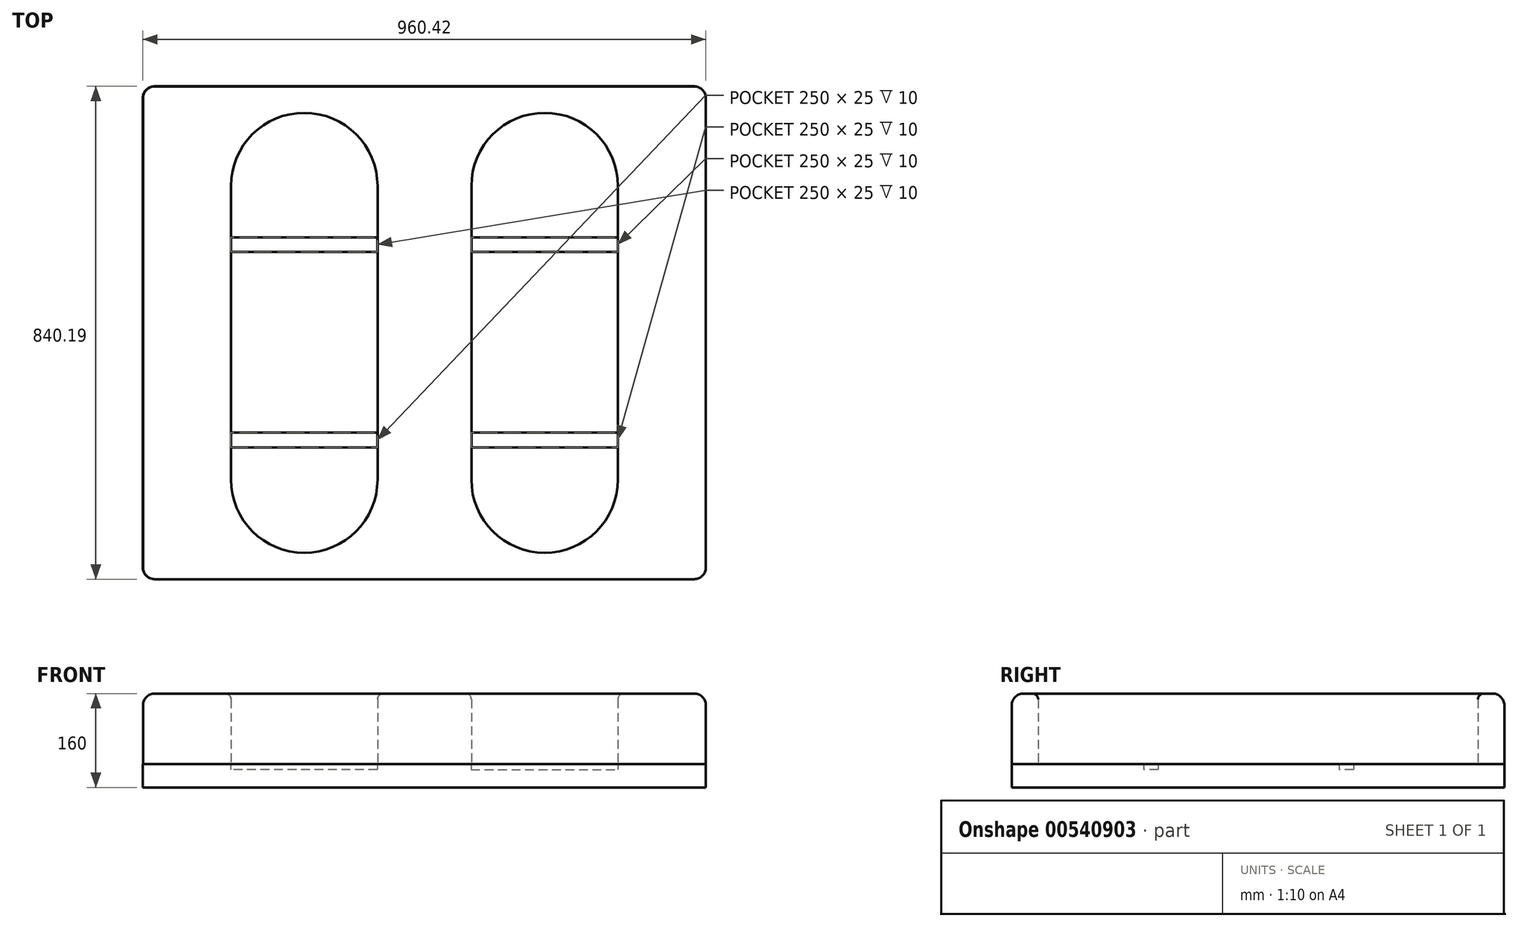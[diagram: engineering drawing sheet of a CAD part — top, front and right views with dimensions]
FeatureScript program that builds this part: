
annotation { "Feature Type Name" : "Feature", "Feature Type Description" : "" }
export const myFeature = defineFeature(function(context is Context, id is Id, definition is map)
    precondition{}
    {
        {
            var Q0;
            Q0=qCreatedBy(makeId("Top.planeOp"),FACE);
            var sketch = newSketch(context, id + "F0", { "sketchPlane" : qUnion([Q0])});
            skLineSegment(sketch, "E0.bottom", {"start": v(-46.58, 670) * mm, "end": v(913.42, 670) * mm});
            skLineSegment(sketch, "E0.top", {"start": v(-46.58, -170) * mm, "end": v(913.42, -170) * mm});
            skLineSegment(sketch, "E0.left", {"start": v(-46.58, 670) * mm, "end": v(-46.58, -170) * mm});
            skLineSegment(sketch, "E0.right", {"start": v(913.42, 670) * mm, "end": v(913.42, -170) * mm});
            skLineSegment(sketch, "E1.left", {"start": v(103.42, 500) * mm, "end": v(103.42, 0) * mm});
            skLineSegment(sketch, "E1.right", {"start": v(353.42, 500) * mm, "end": v(353.42, 0) * mm});
            skLineSegment(sketch, "E2.left", {"start": v(513.42, 500) * mm, "end": v(513.42, 0) * mm});
            skLineSegment(sketch, "E2.right", {"start": v(763.42, 500) * mm, "end": v(763.42, 0) * mm});
            skArc(sketch, "E3", {"start": v(353.42, 500) * mm, "mid": v(228.42, 625) * mm, "end": v(103.42, 500) * mm});
            skArc(sketch, "E4", {"start": v(763.42, 500) * mm, "mid": v(638.42, 625) * mm, "end": v(513.42, 500) * mm});
            skArc(sketch, "E5", {"start": v(513.42, 0) * mm, "mid": v(638.42, -125) * mm, "end": v(763.42, 0) * mm});
            skArc(sketch, "E6", {"start": v(103.42, 0) * mm, "mid": v(228.42, -125) * mm, "end": v(353.42, 0) * mm});
            skLineSegment(sketch, "E7", {"start": v(228.42, 625) * mm, "end": v(228.42, -125) * mm});
            skPoint(sketch, "E7.startSnap0", {"position": v(228.42, 625) * mm});
            skLineSegment(sketch, "E8", {"start": v(638.42, 625) * mm, "end": v(638.42, -125) * mm});
            skLineSegment(sketch, "E9.left", {"start": v(103.42, 420.3) * mm, "end": v(103.42, 420) * mm});
            skLineSegment(sketch, "E9.right", {"start": v(353.42, 420.14) * mm, "end": v(353.42, 419.96) * mm});
            skLineSegment(sketch, "E10.left", {"start": v(103.42, 420.13) * mm, "end": v(103.42, 420.3) * mm});
            skLineSegment(sketch, "E10.right", {"start": v(353.42, 419.78) * mm, "end": v(353.42, 419.96) * mm});
            skSolve(sketch);
        }
        {
            var Q0;
            Q0 = qSketchRegion(id + "F0", true);
            extrude(context, id + "F1", {"entities" : qUnion([Q0]), "depth" : 120 * mm, "offsetDistance" : 25 * mm});
        }
        {
            var Q0;
            Q0=qCreatedBy(makeId("Top.planeOp"),FACE);
            cPlane(context, id + "F2", {"entities" : qUnion([Q0]), "cplaneType" : CPlaneType.OFFSET, "offset" : 40 * mm, "oppositeDirection" : true, "width" : 150 * mm, "height" : 150 * mm});
        }
        {
            var Q0;
            Q0=qCreatedBy(id+"F2.planeOp",FACE);
            var sketch = newSketch(context, id + "F3", { "sketchPlane" : qUnion([Q0])});
            skLineSegment(sketch, "E11.bottom", {"start": v(913, 670.19) * mm, "end": v(-47, 670.19) * mm});
            skLineSegment(sketch, "E11.top", {"start": v(913, -169.81) * mm, "end": v(-47, -169.81) * mm});
            skLineSegment(sketch, "E11.left", {"start": v(913, 670.19) * mm, "end": v(913, -169.81) * mm});
            skLineSegment(sketch, "E11.right", {"start": v(-47, 670.19) * mm, "end": v(-47, -169.81) * mm});
            skLineSegment(sketch, "E12.bottom", {"start": v(103, 79.75) * mm, "end": v(353, 79.75) * mm});
            skLineSegment(sketch, "E12.top", {"start": v(103, 54.75) * mm, "end": v(353, 54.75) * mm});
            skLineSegment(sketch, "E12.left", {"start": v(103, 79.75) * mm, "end": v(103, 54.75) * mm});
            skLineSegment(sketch, "E12.right", {"start": v(353, 79.75) * mm, "end": v(353, 54.75) * mm});
            skLineSegment(sketch, "E13.bottom", {"start": v(513, 79.75) * mm, "end": v(763, 79.75) * mm});
            skLineSegment(sketch, "E13.top", {"start": v(513, 54.75) * mm, "end": v(763, 54.75) * mm});
            skLineSegment(sketch, "E13.left", {"start": v(513, 79.75) * mm, "end": v(513, 54.75) * mm});
            skLineSegment(sketch, "E13.right", {"start": v(763, 79.75) * mm, "end": v(763, 54.75) * mm});
            skLineSegment(sketch, "E14.bottom", {"start": v(513, 412.95) * mm, "end": v(763, 412.95) * mm});
            skLineSegment(sketch, "E14.top", {"start": v(513, 387.95) * mm, "end": v(763, 387.95) * mm});
            skLineSegment(sketch, "E14.left", {"start": v(513, 412.95) * mm, "end": v(513, 387.95) * mm});
            skLineSegment(sketch, "E14.right", {"start": v(763, 412.95) * mm, "end": v(763, 387.95) * mm});
            skLineSegment(sketch, "E15.bottom", {"start": v(353, 412.95) * mm, "end": v(103, 412.95) * mm});
            skLineSegment(sketch, "E15.top", {"start": v(353, 387.95) * mm, "end": v(103, 387.95) * mm});
            skLineSegment(sketch, "E15.left", {"start": v(353, 412.95) * mm, "end": v(353, 387.95) * mm});
            skLineSegment(sketch, "E15.right", {"start": v(103, 412.95) * mm, "end": v(103, 387.95) * mm});
            skSolve(sketch);
        }
        {
            var Q0;
            Q0=makeQuery(id+"F3.imprint","IMPRINT",FACE,{"disambiguationData":[TD([[makeQuery(id+"F3.imprint","IMPRINT",EDGE,{"derivedFrom":sQuery(id+"F3.wireOp",EDGE,"E11.bottom")}),1.0]])]});
            extrude(context, id + "F4", {"entities" : qUnion([Q0]), "depth" : 40 * mm, "offsetDistance" : 25 * mm});
        }
        {
            var Q0;
            Q0=makeQuery(id+"F3.imprint","IMPRINT",FACE,{"disambiguationData":[TD([[makeQuery(id+"F3.imprint","IMPRINT",EDGE,{"derivedFrom":sQuery(id+"F3.wireOp",EDGE,"E15.bottom")}),1.0]])]});
            var Q1;
            Q1=makeQuery(id+"F3.imprint","IMPRINT",FACE,{"disambiguationData":[TD([[makeQuery(id+"F3.imprint","IMPRINT",EDGE,{"derivedFrom":sQuery(id+"F3.wireOp",EDGE,"E14.bottom")}),-1.0]])]});
            var Q2;
            Q2=makeQuery(id+"F3.imprint","IMPRINT",FACE,{"disambiguationData":[TD([[makeQuery(id+"F3.imprint","IMPRINT",EDGE,{"derivedFrom":sQuery(id+"F3.wireOp",EDGE,"E12.bottom")}),-1.0]])]});
            var Q3;
            Q3=makeQuery(id+"F3.imprint","IMPRINT",FACE,{"disambiguationData":[TD([[makeQuery(id+"F3.imprint","IMPRINT",EDGE,{"derivedFrom":sQuery(id+"F3.wireOp",EDGE,"E13.bottom")}),-1.0]])]});
            extrude(context, id + "F5", {"entities" : qUnion([Q0, Q1, Q2, Q3]), "operationType" : NewBodyOperationType.ADD, "depth" : 30 * mm, "offsetDistance" : 25 * mm});
        }
        {
            var Q0;
            Q0=makeQuery(id+"F1.opExtrude","CAP_EDGE",EDGE,{"disambiguationData":[OSD([sQuery(id+"F0.wireOp",EDGE,"E1.right"),sQuery(id+"F0.wireOp",EDGE,"E9.right")])],"isStart":false});
            var Q1;
            Q1=makeQuery(id+"F1.opExtrude","CAP_EDGE",EDGE,{"disambiguationData":[OSD([sQuery(id+"F0.wireOp",EDGE,"E2.right")])],"isStart":false});
            fillet(context, id + "F6", {"entities" : qUnion([Q0, Q1]), "radius" : 10 * mm, "tangentPropagation" : true, "allowEdgeOverflow" : false});
        }
        {
            var Q0;
            Q0=makeQuery(id+"F1.opExtrude","CAP_EDGE",EDGE,{"disambiguationData":[OSD([sQuery(id+"F0.wireOp",EDGE,"E0.top")])],"isStart":false});
            var Q1;
            Q1=makeQuery(id+"F1.opExtrude","CAP_EDGE",EDGE,{"disambiguationData":[OSD([sQuery(id+"F0.wireOp",EDGE,"E0.left")])],"isStart":false});
            var Q2;
            Q2=makeQuery(id+"F1.opExtrude","CAP_EDGE",EDGE,{"disambiguationData":[OSD([sQuery(id+"F0.wireOp",EDGE,"E0.bottom")])],"isStart":false});
            var Q3;
            Q3=makeQuery(id+"F1.opExtrude","CAP_EDGE",EDGE,{"disambiguationData":[OSD([sQuery(id+"F0.wireOp",EDGE,"E0.right")])],"isStart":false});
            var Q4;
            Q4=makeQuery(id+"F1.opExtrude","SWEPT_EDGE",EDGE,{"disambiguationData":[OSD([sQuery(id+"F0.wireOp",EDGE,"E0.top"),sQuery(id+"F0.wireOp",EDGE,"E0.left")])]});
            var Q5;
            Q5=makeQuery(id+"F4.opExtrude","SWEPT_EDGE",EDGE,{"disambiguationData":[OSD([sQuery(id+"F3.wireOp",EDGE,"E11.top"),sQuery(id+"F3.wireOp",EDGE,"E11.right")])]});
            var Q6;
            Q6=makeQuery(id+"F1.opExtrude","SWEPT_EDGE",EDGE,{"disambiguationData":[OSD([sQuery(id+"F0.wireOp",EDGE,"E0.top"),sQuery(id+"F0.wireOp",EDGE,"E0.right")])]});
            var Q7;
            Q7=makeQuery(id+"F4.opExtrude","SWEPT_EDGE",EDGE,{"disambiguationData":[OSD([sQuery(id+"F3.wireOp",EDGE,"E11.top"),sQuery(id+"F3.wireOp",EDGE,"E11.left")])]});
            var Q8;
            Q8=makeQuery(id+"F1.opExtrude","SWEPT_EDGE",EDGE,{"disambiguationData":[OSD([sQuery(id+"F0.wireOp",EDGE,"E0.bottom"),sQuery(id+"F0.wireOp",EDGE,"E0.right")])]});
            var Q9;
            Q9=makeQuery(id+"F4.opExtrude","SWEPT_EDGE",EDGE,{"disambiguationData":[OSD([sQuery(id+"F3.wireOp",EDGE,"E11.bottom"),sQuery(id+"F3.wireOp",EDGE,"E11.left")])]});
            var Q10;
            Q10=makeQuery(id+"F1.opExtrude","SWEPT_EDGE",EDGE,{"disambiguationData":[OSD([sQuery(id+"F0.wireOp",EDGE,"E0.bottom"),sQuery(id+"F0.wireOp",EDGE,"E0.left")])]});
            var Q11;
            Q11=makeQuery(id+"F4.opExtrude","SWEPT_EDGE",EDGE,{"disambiguationData":[OSD([sQuery(id+"F3.wireOp",EDGE,"E11.bottom"),sQuery(id+"F3.wireOp",EDGE,"E11.right")])]});
            fillet(context, id + "F7", {"entities" : qUnion([Q0, Q1, Q2, Q3, Q4, Q5, Q6, Q7, Q8, Q9, Q10, Q11]), "radius" : 20 * mm, "tangentPropagation" : true, "allowEdgeOverflow" : false});
        }
    });
